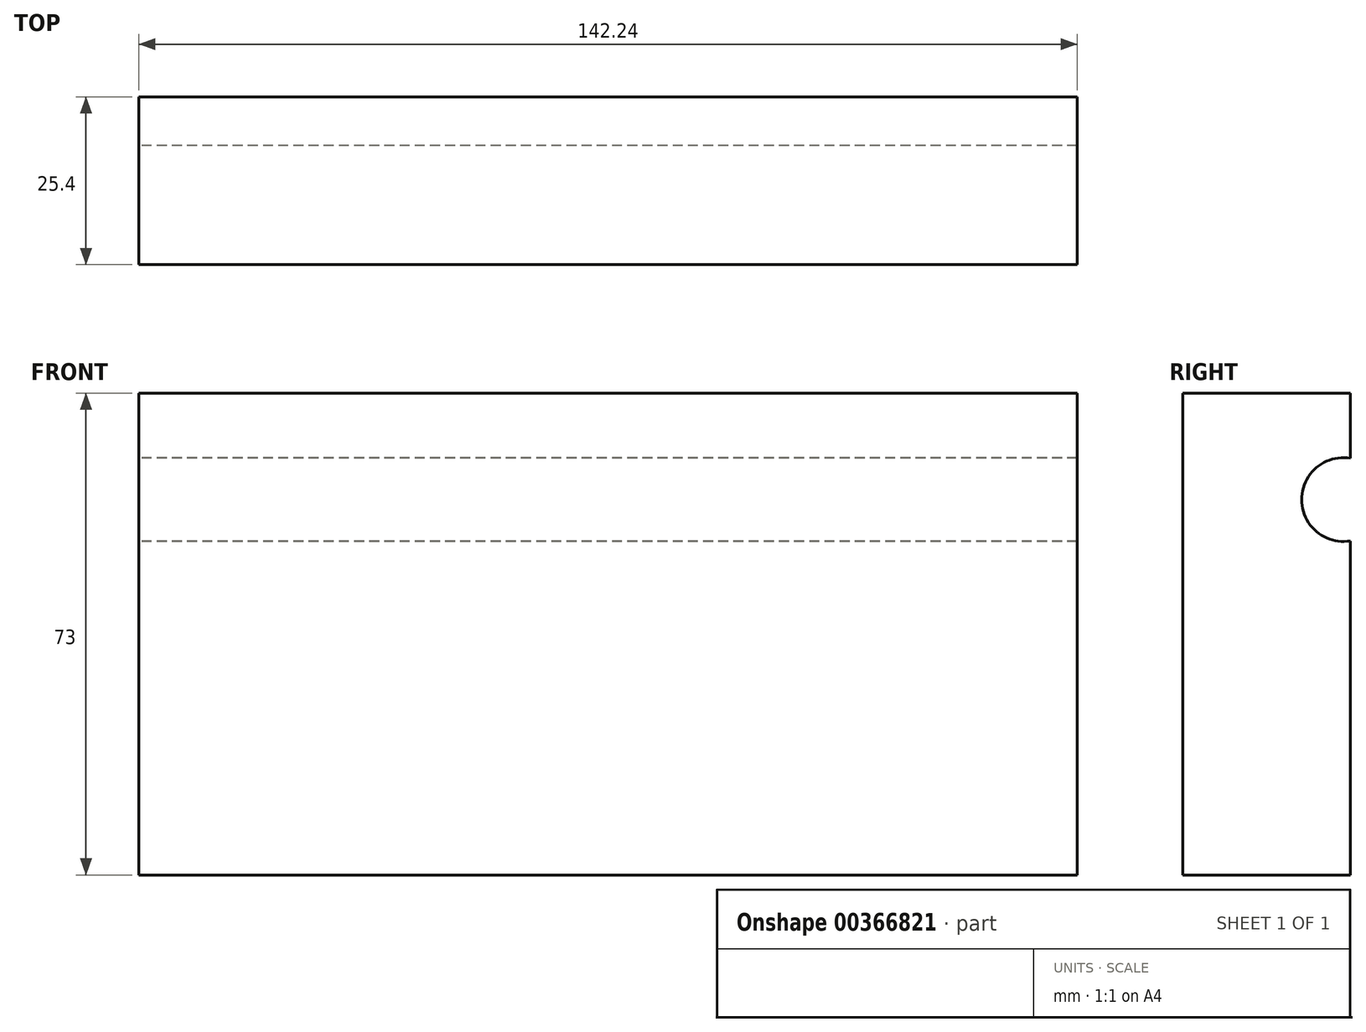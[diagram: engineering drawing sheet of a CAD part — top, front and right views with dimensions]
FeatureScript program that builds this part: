
annotation { "Feature Type Name" : "Feature", "Feature Type Description" : "" }
export const myFeature = defineFeature(function(context is Context, id is Id, definition is map)
    precondition{}
    {
        {
            var Q0;
            Q0=qCreatedBy(makeId("Top.planeOp"),FACE);
            var sketch = newSketch(context, id + "F0", { "sketchPlane" : qUnion([Q0])});
            skLineSegment(sketch, "E0.bottom", {"start": v(-68.18, -1.81) * mm, "end": v(74.06, -1.81) * mm});
            skLineSegment(sketch, "E0.top", {"start": v(-68.18, 36.29) * mm, "end": v(74.06, 36.29) * mm});
            skLineSegment(sketch, "E0.left", {"start": v(-68.18, -1.81) * mm, "end": v(-68.18, 36.29) * mm});
            skLineSegment(sketch, "E0.right", {"start": v(74.06, -1.81) * mm, "end": v(74.06, 36.29) * mm});
            skSolve(sketch);
        }
        {
            var Q0;
            Q0=makeQuery(id+"F0.imprint","IMPRINT",FACE,{"disambiguationData":[TD([[makeQuery(id+"F0.imprint","IMPRINT",EDGE,{"derivedFrom":sQuery(id+"F0.wireOp",EDGE,"E0.bottom")}),1.0]])]});
            extrude(context, id + "F1", {"entities" : qUnion([Q0]), "depth" : 73 * mm});
        }
        {
            var Q0;
            Q0=makeQuery(id+"F1.opExtrude","SWEPT_FACE",FACE,{"disambiguationData":[OSD([sQuery(id+"F0.wireOp",EDGE,"E0.left")])]});
            var sketch = newSketch(context, id + "F2", { "sketchPlane" : qUnion([Q0])});
            skArc(sketch, "E1", {"start": v(-36.29, 50.62) * mm, "mid": v(-28.9, 56.88) * mm, "end": v(-36.29, 63.15) * mm});
            skSolve(sketch);
        }
        {
            var Q0;
            {var subQ0=sQuery(id+"F2.wireOp",EDGE,"E1");Q0=makeQuery(id+"F2.imprint","IMPRINT",FACE,{"disambiguationData":[TD([[makeQuery(id+"F2.imprint","IMPRINT",EDGE,{"derivedFrom":subQ0}),1.0]])]});}
            extrude(context, id + "F3", {"entities" : qUnion([Q0]), "operationType" : NewBodyOperationType.REMOVE, "oppositeDirection" : true, "depth" : 142.24 * mm});
        }
        {
            var Q0;
            Q0=makeQuery(id+"F1.opExtrude","SWEPT_FACE",FACE,{"disambiguationData":[OSD([sQuery(id+"F0.wireOp",EDGE,"E0.bottom")])]});
            extrude(context, id + "F4", {"entities" : qUnion([Q0]), "operationType" : NewBodyOperationType.REMOVE, "oppositeDirection" : true, "depth" : 12.7 * mm});
        }
    });
